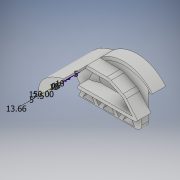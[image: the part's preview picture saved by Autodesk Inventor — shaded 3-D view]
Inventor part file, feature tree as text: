
AUTODESK INVENTOR PART (.ipt)
format: ipt  version: 2017 (Build 210142000, 142)  size: 635,392 bytes
history: native  units: mm
features: sketch x29, extrude x24, plane x7, fillet x4, other x3, revolve x1, boolean_combine x1
ambient origin geometry x8: Origin, YZ Plane, XZ Plane, XY Plane, X Axis, Y Axis, Z Axis, Center Point
bodies: Solid1 (feature_tree), Solid2 (feature_tree)
feature tree (69):
  extrude  "Extrusion1"  Depth=35.0mm
  plane  "Work Plane1"
  extrude  "Extrusion2"  Depth=33.005006mm
  other  "Bend Part1"
  other  "Bend Part2"
  extrude  "Extrusion3"  Depth=32.454mm
  plane  "Work Plane2"
  extrude  "Extrusion4"  Depth=20.0mm
  other  "Bend Part3"
  extrude  "Extrusion5"  Depth=30.0mm
  revolve  "Revolution1"  [1 undecoded]
  plane  "Work Plane3"
  extrude  "Extrusion6"  Depth=10.0mm
  boolean_combine  "Combine1"
  plane  "Work Plane4"
  extrude  "Extrusion7"  TaperAngle=90.0deg  [1 undecoded]
  extrude  "Extrusion8"  Depth=80.0mm
  extrude  "Extrusion9"  Depth=50.0mm TaperAngle=135.0deg
  extrude  "Extrusion10"  Depth=35.0mm
  plane  "Work Plane5"
  extrude  "Extrusion11"  Depth=60.0mm
  extrude  "Extrusion12"  Depth=60.0mm
  plane  "Work Plane6"
  extrude  "Extrusion13"  [1 undecoded]
  extrude  "Extrusion14"  Depth=30.0mm TaperAngle=0.0deg
  plane  "Work Plane7"
  extrude  "Extrusion15"  Depth=20.0mm TaperAngle=0.0deg
  extrude  "Extrusion16"  Depth=15.219936mm
  extrude  "Extrusion17"  Depth=15.155142mm
  fillet  "Fillet1"  Radius=20.0mm
  extrude  "Extrusion18"  Depth=100.334153mm
  fillet  "Fillet2"  Radius=43.193283mm
  fillet  "Fillet3"  Radius=60.0mm
  fillet  "Fillet4"  Radius=60.5mm
  extrude  "Extrusion19"  Depth=25.287025mm
  extrude  "Extrusion20"  Depth=2.439mm TaperAngle=0.0deg
  extrude  "Extrusion21"  Depth=0.980484mm
  extrude  "Extrusion22"  Depth=2.246206mm
  extrude  "Extrusion23"  Depth=100.0mm TaperAngle=0.0deg
  extrude  "Extrusion24"  Depth=5.0mm TaperAngle=0.0deg
  sketch  "Sketch29"  dims[d76=60.0mm d77=60.0mm d78=20.0mm d79=18.461mm d80=116.447mm d81=0.0mm d82=10.0mm d83=8.797686mm d84=116.447mm d85=0.0mm d86=10.0mm d87=9.0mm d88=10.0mm d89=60.197145mm d90=34.482005mm d91=20.0mm d92=3.0mm d93=20.0mm d94=90.0deg d95=55.512917mm d96=23.386841mm d97=11.976391mm d98=75.0mm d99=0.0mm d100=3.0mm d101=20.0mm d102=75.0mm d103=0.0mm d104=14.0mm d105=2.0mm d106=75.0mm d107=0.0mm d108=65.72713mm d109=31.278947mm d110=8.340283mm d111=36.051467mm d112=20.0mm d113=0.0mm d114=10.0mm d115=18.461203mm d116=94.75mm d117=0.0mm d118=1.594016mm d119=1.594016mm d120=11.43616mm d121=30.0mm d123=30.0mm d124=10.0mm d126=10.0mm d128=15.0mm d129=1.594016mm d130=20.0mm d132=30.0mm d133=10.0mm d135=10.0mm d137=10.0mm d138=0.0mm d139=10.0mm d140=5.0mm d141=5.0mm d142=150.0deg d143=30.0mm d145=15.0mm d146=20.0mm d148=15.0mm d151=7.5mm d152=13.66mm d153=30.0mm d155=15.0mm d156=10.0mm d158=10.0mm]
  sketch  "Sketch1"  dims[d0=60.0mm d1=35.0mm]
  sketch  "Sketch2"  dims[d2=60.0mm d3=33.005006mm]
  sketch  "Sketch3"  dims[d4=75.0mm d5=0.0mm d6=32.454mm]
  sketch  "Sketch4"  dims[d7=85.0mm d8=20.0mm]
  sketch  "Sketch5"  dims[d9=5.0mm d10=0.0mm d11=30.0mm]
  sketch  "Sketch6"  dims[d12=55.0mm d13=10.0mm d14=4.363323mm]
  sketch  "Sketch7"  dims[d15=20.0mm d16=10.0mm d17=4.363323mm]
  sketch  "Sketch8"  dims[d18=20.0mm d19=0.0mm d20=90.0deg]
  sketch  "Sketch9"  dims[d21=20.0mm d22=80.0mm]
  sketch  "Sketch10"  dims[d23=5.0mm d24=0.0mm d25=50.0mm d26=135.0deg]
  sketch  "Sketch11"  dims[d27=60.0mm d28=35.0mm]
  sketch  "Sketch12"  dims[d29=35.0mm d30=60.0mm]
  sketch  "Sketch13"  dims[d31=20.0mm d32=0.0mm d33=60.0mm]
  sketch  "Sketch14"  dims[d34=270.0deg d35=-4.697mm]
  sketch  "Sketch15"  dims[d36=20.0mm d37=30.0mm d38=0.0mm]
  sketch  "Sketch16"  dims[d39=-20.0mm d40=20.0mm d41=0.0mm]
  sketch  "Sketch17"  dims[d42=35.67mm d43=15.219936mm]
  sketch  "Sketch18"  dims[d44=35.67mm d45=15.155142mm d46=20.0mm d47=0.0mm]
  sketch  "Sketch19"  dims[d48=20.0mm d49=0.0mm d50=100.334153mm d51=43.193283mm d52=60.0mm d53=0.0mm d54=60.5mm]
  sketch  "Sketch20"  dims[d55=14.497104mm d56=25.287025mm]
  sketch  "Sketch21"  dims[d57=104.0mm d58=0.0mm d59=2.439mm d60=0.0mm]
  sketch  "Sketch22"  dims[d61=-31.25mm d62=0.980484mm]
  sketch  "Sketch23"  dims[d63=1.164325mm d64=2.246206mm]
  sketch  "Sketch24"  dims[d65=25.536883mm d66=100.0mm d67=0.0mm]
  sketch  "Sketch25"  dims[d68=0.0mm d69=5.0mm d70=0.0mm]
  sketch  "Sketch26"  dims[d71=50.209mm]
  sketch  "Sketch27"  dims[d72=95.197mm d73=0.0mm]
  sketch  "Sketch28"  dims[d74=95.197mm d75=0.0mm]
note: 3 required parameter values undecoded (feature->parameter linkage not recoverable at this tier; creation-order binding heuristic only, values carry confidence <= 0.55)